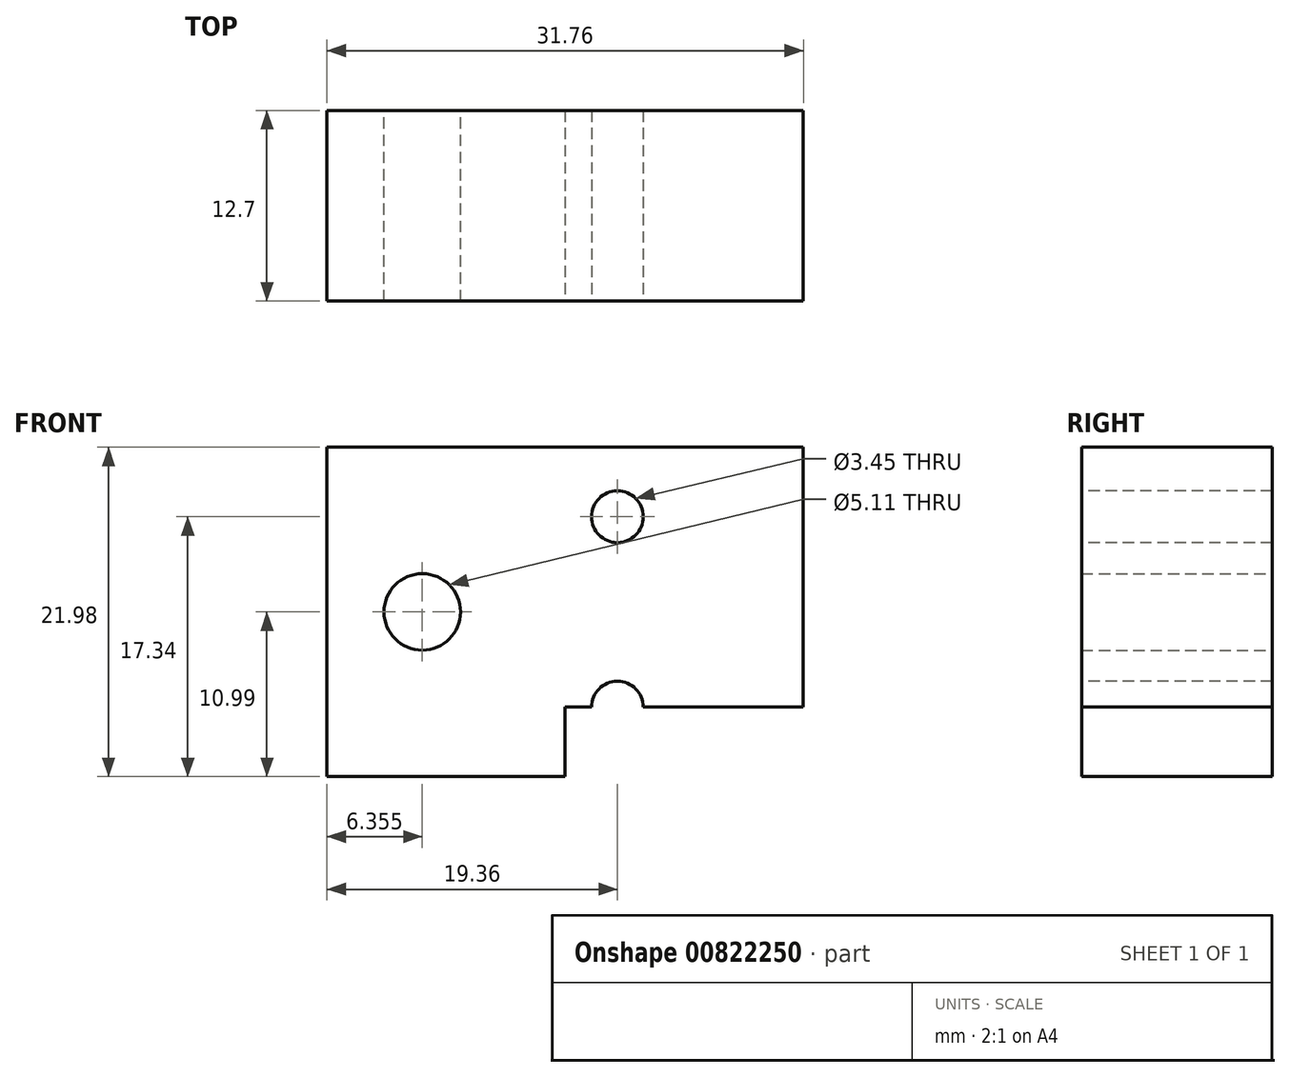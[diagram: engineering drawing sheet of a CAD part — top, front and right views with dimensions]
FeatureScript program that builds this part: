
annotation { "Feature Type Name" : "Feature", "Feature Type Description" : "" }
export const myFeature = defineFeature(function(context is Context, id is Id, definition is map)
    precondition{}
    {
        {
            var Q0;
            Q0=qCreatedBy(makeId("Front.planeOp"),FACE);
            var sketch = newSketch(context, id + "F0", { "sketchPlane" : qUnion([Q0])});
            skLineSegment(sketch, "E0", {"start": v(0, 0) * mm, "end": v(15.88, 0) * mm});
            skLineSegment(sketch, "E1", {"start": v(0, 0) * mm, "end": v(-15.88, 0) * mm});
            skLineSegment(sketch, "E2", {"start": v(0, 0) * mm, "end": v(0, 10.99) * mm});
            skLineSegment(sketch, "E3", {"start": v(0, 0) * mm, "end": v(0, -10.99) * mm});
            skLineSegment(sketch, "E4", {"start": v(0, -10.99) * mm, "end": v(15.88, -10.99) * mm});
            skLineSegment(sketch, "E5", {"start": v(15.88, -10.99) * mm, "end": v(15.88, 10.99) * mm});
            skLineSegment(sketch, "E6", {"start": v(15.88, 10.99) * mm, "end": v(-15.88, 10.99) * mm});
            skLineSegment(sketch, "E7", {"start": v(-15.88, 10.99) * mm, "end": v(-15.88, -10.99) * mm});
            skLineSegment(sketch, "E8", {"start": v(-15.88, -10.99) * mm, "end": v(0, -10.99) * mm});
            skLineSegment(sketch, "E9", {"start": v(0, 0) * mm, "end": v(0, 6.35) * mm});
            skLineSegment(sketch, "E10", {"start": v(0, 6.35) * mm, "end": v(0, -6.35) * mm});
            skLineSegment(sketch, "E11", {"start": v(0, 6.35) * mm, "end": v(15.88, 6.35) * mm});
            skLineSegment(sketch, "E12", {"start": v(0, -6.35) * mm, "end": v(15.88, -6.35) * mm});
            skLineSegment(sketch, "E13", {"start": v(15.88, -6.35) * mm, "end": v(3.48, -6.35) * mm});
            skLineSegment(sketch, "E14", {"start": v(3.48, -6.35) * mm, "end": v(3.48, 6.35) * mm});
            skSolve(sketch);
        }
        {
            var Q0;
            {var subQ1=sQuery(id+"F0.wireOp",EDGE,"E1");Q0=makeQuery(id+"F0.imprint","IMPRINT",FACE,{"disambiguationData":[TD([[makeQuery(id+"F0.imprint","IMPRINT",EDGE,{"derivedFrom":subQ1}),1.0]])]});}
            var Q1;
            {var subQ4=sQuery(id+"F0.wireOp",EDGE,"E1");Q1=makeQuery(id+"F0.imprint","IMPRINT",FACE,{"disambiguationData":[TD([[makeQuery(id+"F0.imprint","IMPRINT",EDGE,{"derivedFrom":subQ4}),-1.0]])]});}
            var Q2;
            {var subQ1=sQuery(id+"F0.wireOp",EDGE,"E2");Q2=makeQuery(id+"F0.imprint","IMPRINT",FACE,{"disambiguationData":[TD([[makeQuery(id+"F0.imprint","IMPRINT",EDGE,{"derivedFrom":subQ1}),-1.0]])]});}
            var Q3;
            {var subQ0=sQuery(id+"F0.wireOp",EDGE,"E14");var subQ1=sQuery(id+"F0.wireOp",EDGE,"E0");var subQ2=makeQuery(id+"F0.imprint","INTERSECT",VERTEX,{"derivedFrom":[subQ1,subQ0]});Q3=makeQuery(id+"F0.imprint","IMPRINT",FACE,{"disambiguationData":[TD([[makeQuery(id+"F0.imprint","IMPRINT",EDGE,{"disambiguationData":[TD([[subQ2,-1.0]])],"derivedFrom":subQ0}),1.0]])]});}
            var Q4;
            {var subQ1=sQuery(id+"F0.wireOp",EDGE,"E0");var subQ6=sQuery(id+"F0.wireOp",EDGE,"E5");var subQ9=makeQuery(id+"F0.imprint","INTERSECT",VERTEX,{"derivedFrom":[subQ1,subQ6]});Q4=makeQuery(id+"F0.imprint","IMPRINT",FACE,{"disambiguationData":[TD([[makeQuery(id+"F0.imprint","IMPRINT",EDGE,{"disambiguationData":[TD([[subQ9,1.0]])],"derivedFrom":subQ1}),1.0]])]});}
            var Q5;
            {var subQ1=sQuery(id+"F0.wireOp",EDGE,"E5");var subQ5=sQuery(id+"F0.wireOp",EDGE,"E0");var subQ6=makeQuery(id+"F0.imprint","INTERSECT",VERTEX,{"derivedFrom":[subQ5,subQ1]});Q5=makeQuery(id+"F0.imprint","IMPRINT",FACE,{"disambiguationData":[TD([[makeQuery(id+"F0.imprint","IMPRINT",EDGE,{"disambiguationData":[TD([[subQ6,1.0]])],"derivedFrom":subQ5}),-1.0]])]});}
            var Q6;
            {var subQ0=sQuery(id+"F0.wireOp",EDGE,"E14");var subQ1=sQuery(id+"F0.wireOp",EDGE,"E0");var subQ2=makeQuery(id+"F0.imprint","INTERSECT",VERTEX,{"derivedFrom":[subQ1,subQ0]});Q6=makeQuery(id+"F0.imprint","IMPRINT",FACE,{"disambiguationData":[TD([[makeQuery(id+"F0.imprint","IMPRINT",EDGE,{"disambiguationData":[TD([[subQ2,1.0]])],"derivedFrom":subQ0}),1.0]])]});}
            var Q7;
            {var subQ1=sQuery(id+"F0.wireOp",EDGE,"E3");Q7=makeQuery(id+"F0.imprint","IMPRINT",FACE,{"disambiguationData":[TD([[makeQuery(id+"F0.imprint","IMPRINT",EDGE,{"derivedFrom":subQ1}),1.0]])]});}
            var Q8;
            {var subQ1=sQuery(id+"F0.wireOp",EDGE,"E12");var subQ3=sQuery(id+"F0.wireOp",EDGE,"MIaaSfoV-tMlf-iQDG-LgLp-gHh0eWpWpbag");var subQ4=makeQuery(id+"F0.imprint","INTERSECT",VERTEX,{"derivedFrom":[subQ1,subQ3]});Q8=makeQuery(id+"F0.imprint","IMPRINT",FACE,{"disambiguationData":[TD([[makeQuery(id+"F0.imprint","IMPRINT",EDGE,{"disambiguationData":[TD([[subQ4,-1.0]])],"derivedFrom":subQ3}),1.0]])]});}
            var Q9;
            {var subQ1=sQuery(id+"F0.wireOp",EDGE,"E12");var subQ3=sQuery(id+"F0.wireOp",EDGE,"MIaaSfoV-tMlf-iQDG-LgLp-gHh0eWpWpbag");var subQ4=makeQuery(id+"F0.imprint","INTERSECT",VERTEX,{"derivedFrom":[subQ1,subQ3]});Q9=makeQuery(id+"F0.imprint","IMPRINT",FACE,{"disambiguationData":[TD([[makeQuery(id+"F0.imprint","IMPRINT",EDGE,{"disambiguationData":[TD([[subQ4,1.0]])],"derivedFrom":subQ3}),1.0]])]});}
            var Q10;
            {var subQ1=sQuery(id+"F0.wireOp",EDGE,"E13");var subQ3=sQuery(id+"F0.wireOp",EDGE,"MIaaSfoV-tMlf-iQDG-LgLp-gHh0eWpWpbag");var subQ4=makeQuery(id+"F0.imprint","INTERSECT",VERTEX,{"derivedFrom":[subQ1,subQ3]});Q10=makeQuery(id+"F0.imprint","IMPRINT",FACE,{"disambiguationData":[TD([[makeQuery(id+"F0.imprint","IMPRINT",EDGE,{"disambiguationData":[TD([[subQ4,-1.0]])],"derivedFrom":subQ3}),1.0]])]});}
            var Q11;
            {var subQ0=sQuery(id+"F0.wireOp",EDGE,"E14");var subQ1=sQuery(id+"F0.wireOp",EDGE,"E11");var subQ2=makeQuery(id+"F0.imprint","INTERSECT",VERTEX,{"derivedFrom":[subQ1,subQ0]});Q11=makeQuery(id+"F0.imprint","IMPRINT",FACE,{"disambiguationData":[TD([[makeQuery(id+"F0.imprint","IMPRINT",EDGE,{"disambiguationData":[TD([[subQ2,-1.0]])],"derivedFrom":subQ1}),-1.0]])]});}
            var Q12;
            {var subQ0=sQuery(id+"F0.wireOp",EDGE,"E14");var subQ1=sQuery(id+"F0.wireOp",EDGE,"E11");var subQ2=makeQuery(id+"F0.imprint","INTERSECT",VERTEX,{"derivedFrom":[subQ1,subQ0]});Q12=makeQuery(id+"F0.imprint","IMPRINT",FACE,{"disambiguationData":[TD([[makeQuery(id+"F0.imprint","IMPRINT",EDGE,{"disambiguationData":[TD([[subQ2,1.0]])],"derivedFrom":subQ1}),-1.0]])]});}
            var Q13;
            {var subQ0=sQuery(id+"F0.wireOp",EDGE,"E11");var subQ1=makeQuery(id+"F0.imprint","INTERSECT",VERTEX,{"derivedFrom":[subQ0,sQuery(id+"F0.wireOp",EDGE,"E14")]});Q13=makeQuery(id+"F0.imprint","IMPRINT",FACE,{"disambiguationData":[TD([[makeQuery(id+"F0.imprint","IMPRINT",EDGE,{"disambiguationData":[TD([[subQ1,1.0]])],"derivedFrom":subQ0}),1.0]])]});}
            extrude(context, id + "F1", {"entities" : qUnion([Q0, Q1, Q2, Q3, Q4, Q5, Q6, Q7, Q8, Q9, Q10, Q11, Q12, Q13]), "oppositeDirection" : true, "depth" : 12.7 * mm, "offsetDistance" : 25.4 * mm});
        }
        {
            var Q0;
            Q0=sQuery(id+"F0.wireOp",VERTEX,"E13.end");
            var Q1;
            Q1=sQuery(id+"F0.wireOp",VERTEX,"E14.end");
            var Q2;
            Q2=makeQuery(id+"F1.opExtrude","SWEPT_BODY",BODY,{"disambiguationData":[OSD([sQuery(id+"F0.wireOp",EDGE,"E4"),sQuery(id+"F0.wireOp",EDGE,"E5"),sQuery(id+"F0.wireOp",EDGE,"E6"),sQuery(id+"F0.wireOp",EDGE,"E7"),sQuery(id+"F0.wireOp",EDGE,"E8")])]});
            hole(context, id + "F2", {"style" : HoleStyle.SIMPLE, "endStyle" : HoleEndStyle.THROUGH, "standardTappedOrClearance" : lookupTablePath({ "standard" : "ANSI", "engagement" : "75%", "pitch" : "32 tpi", "size" : "#8", "type" : "Tapped" }), "standardBlindInLast" : lookupTablePath({ "standard" : "ANSI", "engagement" : "75%", "pitch" : "32 tpi", "size" : "#8", "type" : "Tapped" }), "holeDiameter" : 3.45 * mm, "majorDiameter" : 4.17 * mm, "showTappedDepth" : true, "isTappedThrough" : true, "tappedDepth" : 12.7 * mm, "tapClearance" : 3, "locations" : qUnion([Q0, Q1]), "scope" : qUnion([Q2])});
        }
        {
            var Q0;
            Q0=makeQuery(id+"F1.opExtrude","CAP_FACE",FACE,{"disambiguationData":[OSD([sQuery(id+"F0.wireOp",EDGE,"E4"),sQuery(id+"F0.wireOp",EDGE,"E5"),sQuery(id+"F0.wireOp",EDGE,"E6"),sQuery(id+"F0.wireOp",EDGE,"E7"),sQuery(id+"F0.wireOp",EDGE,"E8")])],"isStart":false});
            var sketch = newSketch(context, id + "F3", { "sketchPlane" : qUnion([Q0])});
            skLineSegment(sketch, "E15", {"start": v(-15.88, 0) * mm, "end": v(9.53, 0) * mm});
            skSolve(sketch);
        }
        {
            var Q0;
            Q0=sQuery(id+"F3.wireOp",VERTEX,"E15.end");
            var Q1;
            Q1=makeQuery(id+"F1.opExtrude","SWEPT_BODY",BODY,{"disambiguationData":[OSD([sQuery(id+"F0.wireOp",EDGE,"E4"),sQuery(id+"F0.wireOp",EDGE,"E5"),sQuery(id+"F0.wireOp",EDGE,"E6"),sQuery(id+"F0.wireOp",EDGE,"E7"),sQuery(id+"F0.wireOp",EDGE,"E8")])]});
            hole(context, id + "F4", {"style" : HoleStyle.SIMPLE, "endStyle" : HoleEndStyle.THROUGH, "standardTappedOrClearance" : lookupTablePath({ "standard" : "ANSI", "engagement" : "75%", "pitch" : "20 tpi", "size" : "1/4", "type" : "Tapped" }), "standardBlindInLast" : lookupTablePath({ "standard" : "ANSI", "engagement" : "75%", "pitch" : "20 tpi", "size" : "1/4", "type" : "Tapped" }), "holeDiameter" : 5.1 * mm, "majorDiameter" : 6.35 * mm, "showTappedDepth" : true, "isTappedThrough" : true, "tappedDepth" : 12.7 * mm, "tapClearance" : 3, "locations" : qUnion([Q0]), "scope" : qUnion([Q1])});
        }
    });
